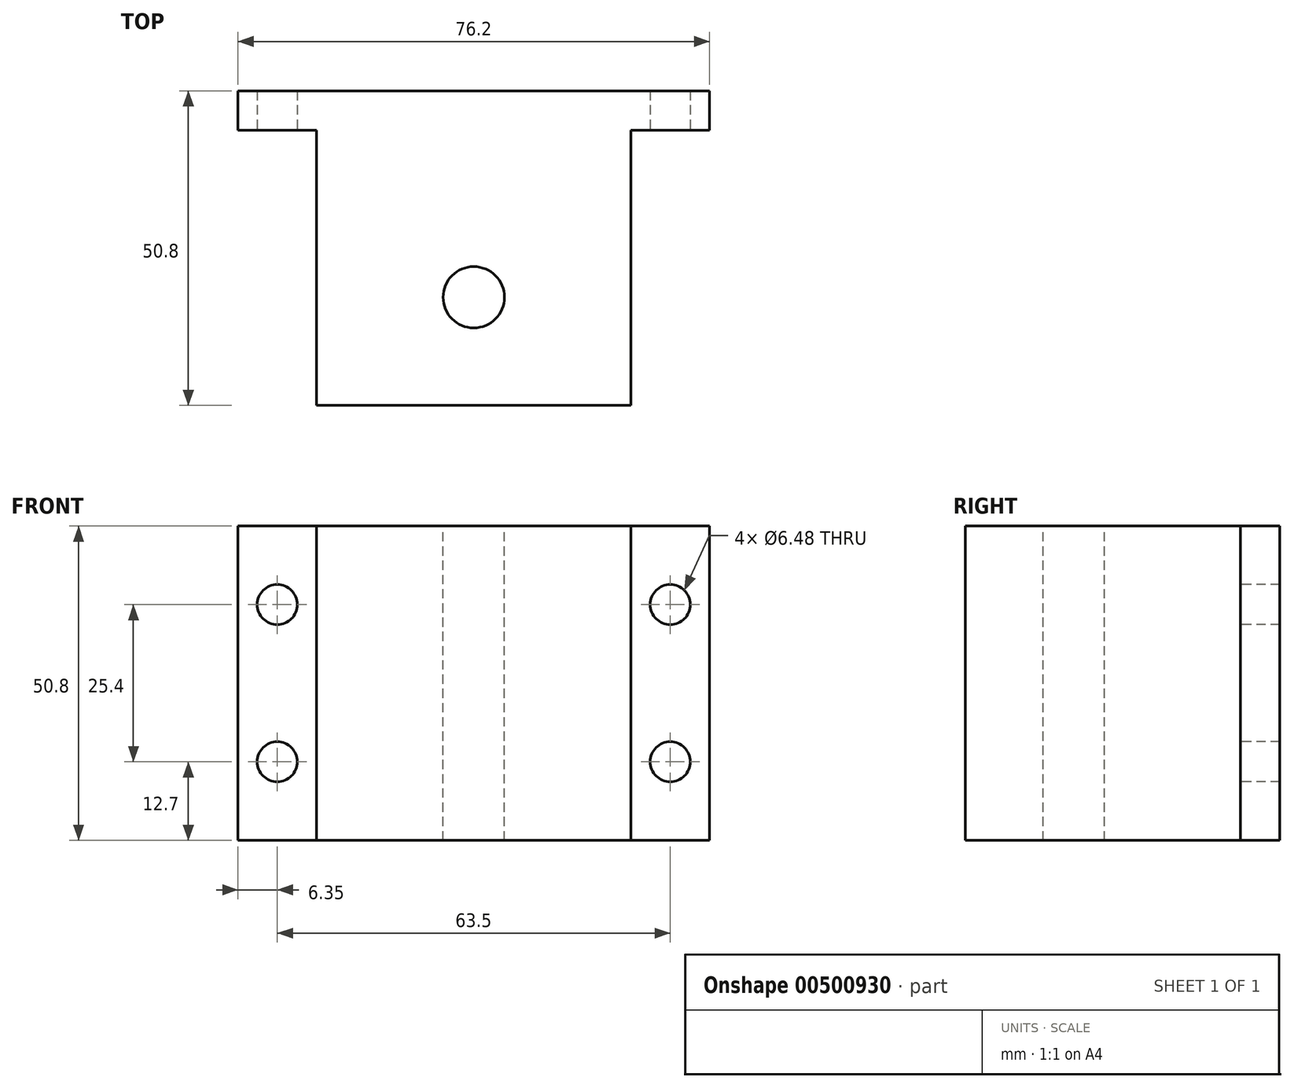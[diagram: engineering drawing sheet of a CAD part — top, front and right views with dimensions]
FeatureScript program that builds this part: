
annotation { "Feature Type Name" : "Feature", "Feature Type Description" : "" }
export const myFeature = defineFeature(function(context is Context, id is Id, definition is map)
    precondition{}
    {
        {
            var Q0;
            Q0=qCreatedBy(makeId("Top.planeOp"),FACE);
            var sketch = newSketch(context, id + "F0", { "sketchPlane" : qUnion([Q0])});
            skLineSegment(sketch, "E0", {"start": v(0, 0) * mm, "end": v(-76.2, 0) * mm});
            skLineSegment(sketch, "E1", {"start": v(-76.2, 0) * mm, "end": v(-76.2, -6.35) * mm});
            skLineSegment(sketch, "E2", {"start": v(-76.2, -6.35) * mm, "end": v(-63.5, -6.35) * mm});
            skLineSegment(sketch, "E3", {"start": v(-63.5, -6.35) * mm, "end": v(-63.5, -50.8) * mm});
            skLineSegment(sketch, "E4", {"start": v(-63.5, -50.8) * mm, "end": v(-12.7, -50.8) * mm});
            skLineSegment(sketch, "E5", {"start": v(-12.7, -50.8) * mm, "end": v(-12.7, -6.35) * mm});
            skLineSegment(sketch, "E6", {"start": v(-12.7, -6.35) * mm, "end": v(0, -6.35) * mm});
            skLineSegment(sketch, "E7", {"start": v(0, -6.35) * mm, "end": v(0, 0) * mm});
            skSolve(sketch);
        }
        {
            var Q0;
            Q0=makeQuery(id+"F0.imprint","IMPRINT",FACE,{"disambiguationData":[TD([[makeQuery(id+"F0.imprint","IMPRINT",EDGE,{"derivedFrom":sQuery(id+"F0.wireOp",EDGE,"E0")}),1.0]])]});
            extrude(context, id + "F1", {"entities" : qUnion([Q0]), "depth" : 50.8 * mm, "offsetDistance" : 25.4 * mm});
        }
        {
            var Q0;
            Q0=makeQuery(id+"F1.opExtrude","CAP_FACE",FACE,{"disambiguationData":[OSD([sQuery(id+"F0.wireOp",EDGE,"E0"),sQuery(id+"F0.wireOp",EDGE,"E1"),sQuery(id+"F0.wireOp",EDGE,"E2"),sQuery(id+"F0.wireOp",EDGE,"E3"),sQuery(id+"F0.wireOp",EDGE,"E4"),sQuery(id+"F0.wireOp",EDGE,"E5"),sQuery(id+"F0.wireOp",EDGE,"E6"),sQuery(id+"F0.wireOp",EDGE,"E7")])],"isStart":false});
            var sketch = newSketch(context, id + "F2", { "sketchPlane" : qUnion([Q0])});
            skCircle(sketch, "E8", {"center": v(-38.1, -33.34) * mm, "radius": 4.95 * mm});
            skSolve(sketch);
        }
        {
            var Q0;
            Q0=makeQuery(id+"F2.imprint","IMPRINT",FACE,{"disambiguationData":[TD([[makeQuery(id+"F2.imprint","IMPRINT",EDGE,{"derivedFrom":sQuery(id+"F2.wireOp",EDGE,"E8")}),1.0]])]});
            extrude(context, id + "F3", {"entities" : qUnion([Q0]), "operationType" : NewBodyOperationType.REMOVE, "oppositeDirection" : true, "depth" : 50.8 * mm, "offsetDistance" : 25.4 * mm});
        }
        {
            var Q0;
            Q0=makeQuery(id+"F1.opExtrude","SWEPT_FACE",FACE,{"disambiguationData":[OSD([sQuery(id+"F0.wireOp",EDGE,"E6")])]});
            var sketch = newSketch(context, id + "F4", { "sketchPlane" : qUnion([Q0])});
            skCircle(sketch, "E9", {"center": v(-6.35, 12.7) * mm, "radius": 3.24 * mm});
            skCircle(sketch, "E10", {"center": v(-6.35, 38.1) * mm, "radius": 3.24 * mm});
            skSolve(sketch);
        }
        {
            var Q0;
            Q0=makeQuery(id+"F1.opExtrude","SWEPT_FACE",FACE,{"disambiguationData":[OSD([sQuery(id+"F0.wireOp",EDGE,"E2")])]});
            var sketch = newSketch(context, id + "F5", { "sketchPlane" : qUnion([Q0])});
            skCircle(sketch, "E11", {"center": v(-69.85, 12.7) * mm, "radius": 3.24 * mm});
            skCircle(sketch, "E12", {"center": v(-69.85, 38.1) * mm, "radius": 3.24 * mm});
            skSolve(sketch);
        }
        {
            var Q0;
            Q0=makeQuery(id+"F5.imprint","IMPRINT",FACE,{"disambiguationData":[TD([[makeQuery(id+"F5.imprint","IMPRINT",EDGE,{"derivedFrom":sQuery(id+"F5.wireOp",EDGE,"E11")}),1.0]])]});
            var Q1;
            Q1=makeQuery(id+"F4.imprint","IMPRINT",FACE,{"disambiguationData":[TD([[makeQuery(id+"F4.imprint","IMPRINT",EDGE,{"derivedFrom":sQuery(id+"F4.wireOp",EDGE,"E9")}),1.0]])]});
            var Q2;
            Q2=makeQuery(id+"F5.imprint","IMPRINT",FACE,{"disambiguationData":[TD([[makeQuery(id+"F5.imprint","IMPRINT",EDGE,{"derivedFrom":sQuery(id+"F5.wireOp",EDGE,"E12")}),1.0]])]});
            var Q3;
            Q3=makeQuery(id+"F4.imprint","IMPRINT",FACE,{"disambiguationData":[TD([[makeQuery(id+"F4.imprint","IMPRINT",EDGE,{"derivedFrom":sQuery(id+"F4.wireOp",EDGE,"E10")}),1.0]])]});
            extrude(context, id + "F6", {"entities" : qUnion([Q0, Q1, Q2, Q3]), "operationType" : NewBodyOperationType.REMOVE, "oppositeDirection" : true, "depth" : 25.4 * mm, "offsetDistance" : 25.4 * mm});
        }
    });
